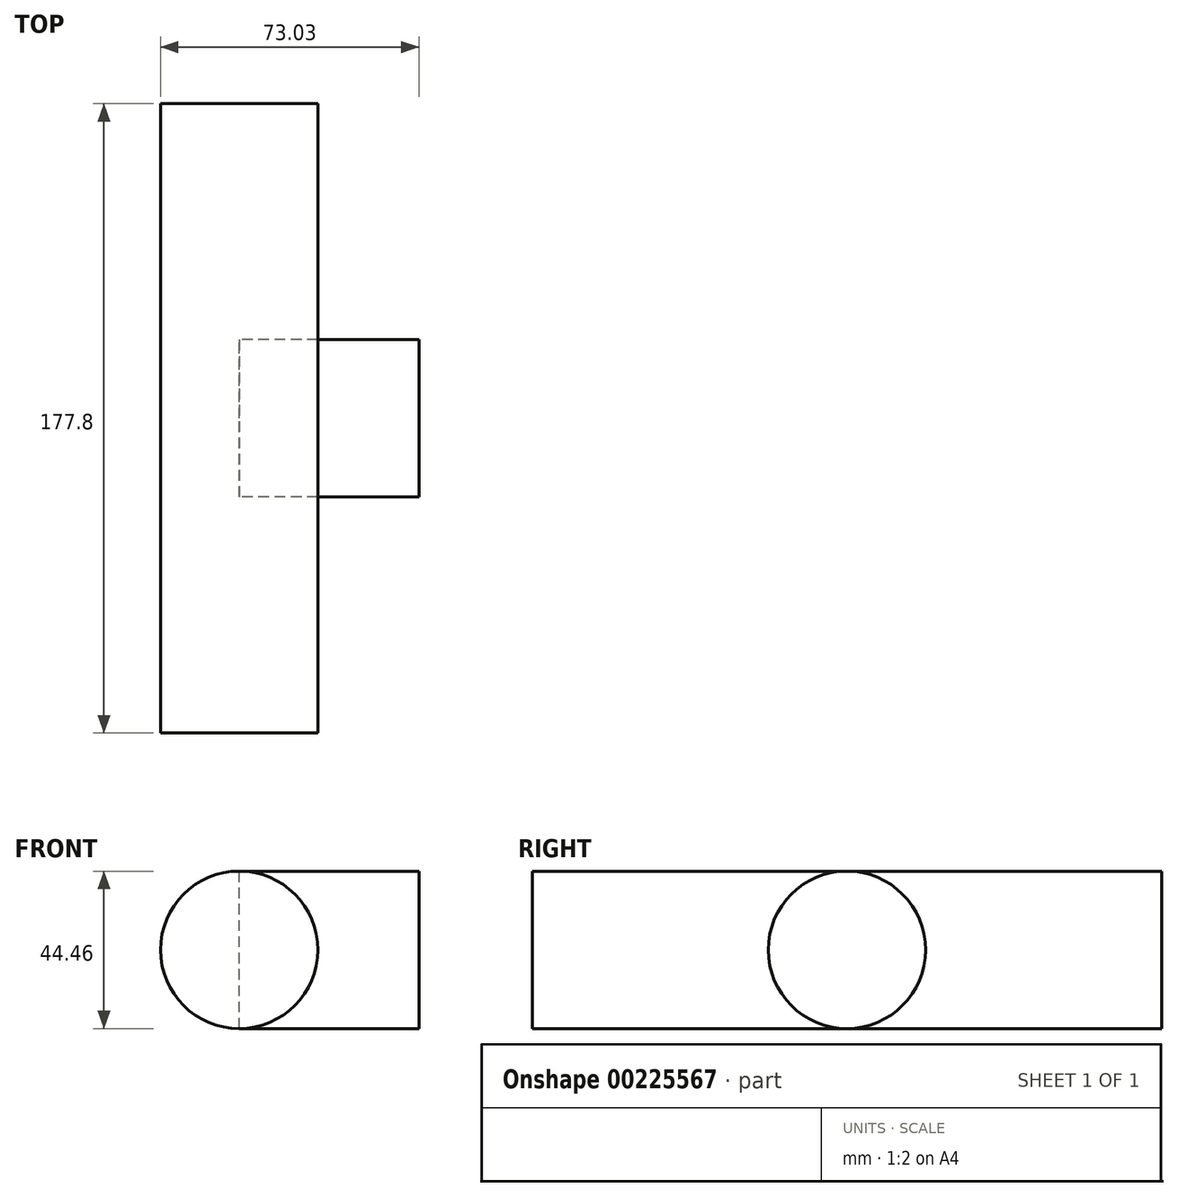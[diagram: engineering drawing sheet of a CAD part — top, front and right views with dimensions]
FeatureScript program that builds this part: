
annotation { "Feature Type Name" : "Feature", "Feature Type Description" : "" }
export const myFeature = defineFeature(function(context is Context, id is Id, definition is map)
    precondition{}
    {
        {
            var Q0;
            Q0=qCreatedBy(makeId("Front.planeOp"),FACE);
            var sketch = newSketch(context, id + "F0", { "sketchPlane" : qUnion([Q0])});
            skCircle(sketch, "E0", {"center": v(0, 0) * mm, "radius": 22.23 * mm});
            skSolve(sketch);
        }
        {
            var Q0;
            Q0=makeQuery(id+"F0.imprint","IMPRINT",FACE,{"disambiguationData":[TD([[makeQuery(id+"F0.imprint","IMPRINT",EDGE,{"derivedFrom":sQuery(id+"F0.wireOp",EDGE,"E0")}),1.0]])]});
            var Q1;
            Q1=sQuery(id+"F0.wireOp",EDGE,"E0");
            extrude(context, id + "F1", {"entities" : qUnion([Q0]), "surfaceEntities" : qUnion([Q1]), "endBound" : BoundingType.SYMMETRIC, "depth" : 177.8 * mm});
        }
        {
            var Q0;
            Q0=qCreatedBy(makeId("Right.planeOp"),FACE);
            var sketch = newSketch(context, id + "F2", { "sketchPlane" : qUnion([Q0])});
            skCircle(sketch, "E1", {"center": v(0, 0) * mm, "radius": 22.23 * mm});
            skSolve(sketch);
        }
        {
            var Q0;
            Q0 = qSketchRegion(id + "F2", true);
            extrude(context, id + "F3", {"entities" : qUnion([Q0]), "depth" : 50.8 * mm});
        }
    });
